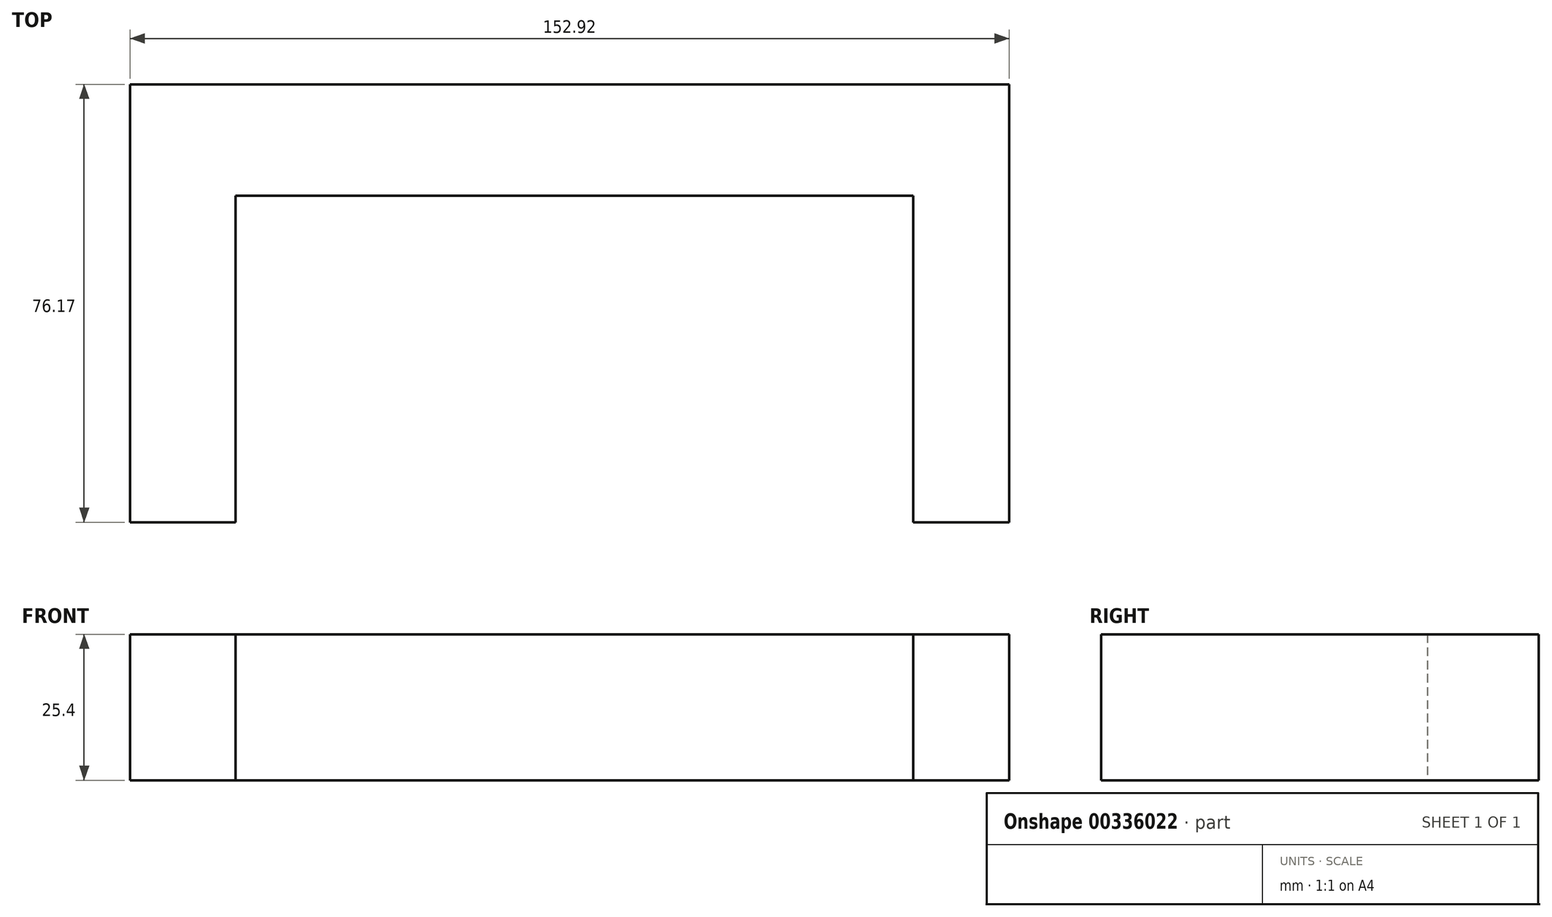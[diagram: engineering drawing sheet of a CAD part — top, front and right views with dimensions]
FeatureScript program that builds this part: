
annotation { "Feature Type Name" : "Feature", "Feature Type Description" : "" }
export const myFeature = defineFeature(function(context is Context, id is Id, definition is map)
    precondition{}
    {
        {
            var Q0;
            Q0=qCreatedBy(makeId("Top.planeOp"),FACE);
            var sketch = newSketch(context, id + "F0", { "sketchPlane" : qUnion([Q0])});
            skLineSegment(sketch, "E0", {"start": v(-75.64, 0) * mm, "end": v(-75.64, 76.17) * mm});
            skLineSegment(sketch, "E1", {"start": v(-75.64, 76.17) * mm, "end": v(77.28, 76.17) * mm});
            skLineSegment(sketch, "E2", {"start": v(77.28, 76.17) * mm, "end": v(77.28, 0) * mm});
            skLineSegment(sketch, "E3", {"start": v(-75.64, 0) * mm, "end": v(-57.3, 0) * mm});
            skLineSegment(sketch, "E4", {"start": v(-57.3, 0) * mm, "end": v(-57.3, 56.81) * mm});
            skLineSegment(sketch, "E5", {"start": v(-57.3, 56.81) * mm, "end": v(60.58, 56.81) * mm});
            skLineSegment(sketch, "E6", {"start": v(60.58, 56.81) * mm, "end": v(60.58, 0) * mm});
            skLineSegment(sketch, "E7", {"start": v(60.58, 0) * mm, "end": v(77.28, 0) * mm});
            skSolve(sketch);
        }
        {
            var Q0;
            Q0 = qSketchRegion(id + "F0", true);
            var Q1;
            Q1=makeQuery(id+"F0.imprint","IMPRINT",FACE,{"disambiguationData":[TD([[makeQuery(id+"F0.imprint","IMPRINT",EDGE,{"derivedFrom":sQuery(id+"F0.wireOp",EDGE,"E0")}),-1.0]])]});
            extrude(context, id + "F1", {"entities" : qUnion([Q0, Q1]), "depth" : 25.4 * mm});
        }
    });
